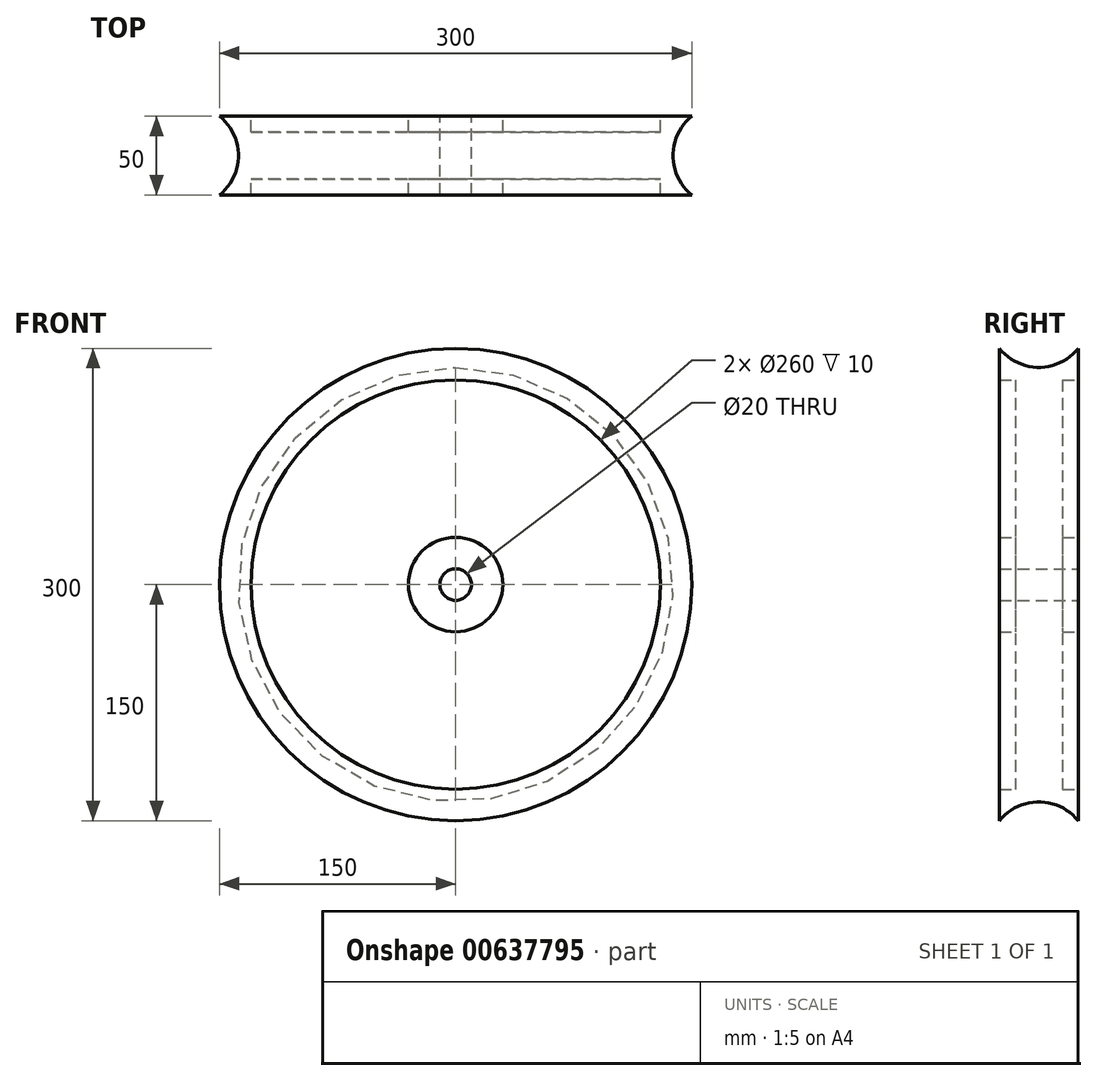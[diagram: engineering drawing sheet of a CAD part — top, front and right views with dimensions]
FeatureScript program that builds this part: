
annotation { "Feature Type Name" : "Feature", "Feature Type Description" : "" }
export const myFeature = defineFeature(function(context is Context, id is Id, definition is map)
    precondition{}
    {
        {
            var Q0;
            Q0=qCreatedBy(makeId("Top.planeOp"),FACE);
            var sketch = newSketch(context, id + "F0", { "sketchPlane" : qUnion([Q0])});
            skLineSegment(sketch, "E0", {"start": v(10, 25) * mm, "end": v(10, -25) * mm});
            skLineSegment(sketch, "E1", {"start": v(10, 25) * mm, "end": v(10, 0) * mm, "construction": true});
            skLineSegment(sketch, "E2", {"start": v(0, 0) * mm, "end": v(10, 0) * mm, "construction": true});
            skLineSegment(sketch, "E3", {"start": v(10, 0) * mm, "end": v(10, -25) * mm});
            skLineSegment(sketch, "E4", {"start": v(10, 25) * mm, "end": v(30, 25) * mm});
            skLineSegment(sketch, "E5", {"start": v(10, -25) * mm, "end": v(30, -25) * mm});
            skLineSegment(sketch, "E6", {"start": v(30, 25) * mm, "end": v(30, 15) * mm});
            skLineSegment(sketch, "E7", {"start": v(30, -15) * mm, "end": v(30, -25) * mm});
            skLineSegment(sketch, "E8", {"start": v(30, 15) * mm, "end": v(130, 15) * mm});
            skLineSegment(sketch, "E9", {"start": v(30, -15) * mm, "end": v(130, -15) * mm});
            skLineSegment(sketch, "E10", {"start": v(130, 15) * mm, "end": v(130, 25) * mm});
            skLineSegment(sketch, "E11", {"start": v(130, -15) * mm, "end": v(130, -25) * mm});
            skLineSegment(sketch, "E12", {"start": v(130, 25) * mm, "end": v(150, 25) * mm});
            skLineSegment(sketch, "E13", {"start": v(130, -25) * mm, "end": v(150, -25) * mm});
            skArc(sketch, "E14", {"start": v(150, 25) * mm, "mid": v(138, 0) * mm, "end": v(150, -25) * mm});
            skLineSegment(sketch, "E15", {"start": v(0, 40.06) * mm, "end": v(0, -44.72) * mm, "construction": true});
            skLineSegment(sketch, "E16", {"start": v(10, 25) * mm, "end": v(0, 25) * mm, "construction": true});
            skSolve(sketch);
        }
        {
            var Q0;
            Q0 = qSketchRegion(id + "F0", true);
            var Q1;
            Q1=sQuery(id+"F0.wireOp",EDGE,"E15");
            revolve(context, id + "F1", {"surfaceOperationType" : NewSurfaceOperationType.NEW, "entities" : qUnion([Q0]), "axis" : qUnion([Q1]), "revolveType" : RevolveType.FULL});
        }
    });
